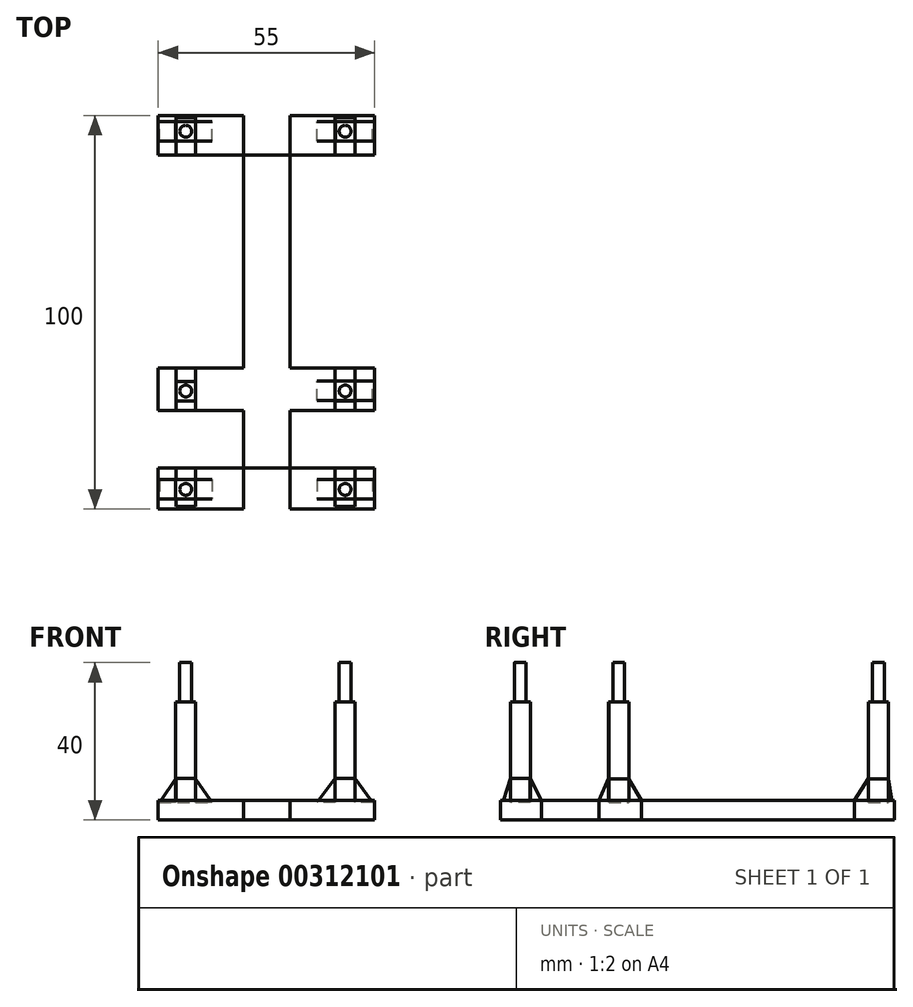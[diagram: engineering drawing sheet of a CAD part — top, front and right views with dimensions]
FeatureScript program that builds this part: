
annotation { "Feature Type Name" : "Feature", "Feature Type Description" : "" }
export const myFeature = defineFeature(function(context is Context, id is Id, definition is map)
    precondition{}
    {
        {
            var Q0;
            Q0=qCreatedBy(makeId("Top.planeOp"),FACE);
            var sketch = newSketch(context, id + "F0", { "sketchPlane" : qUnion([Q0])});
            skLineSegment(sketch, "E0.bottom", {"start": v(27.5, -50) * mm, "end": v(-27.5, -50) * mm});
            skLineSegment(sketch, "E0.top", {"start": v(27.5, 50) * mm, "end": v(-27.5, 50) * mm});
            skLineSegment(sketch, "E0.left", {"start": v(27.5, -50) * mm, "end": v(27.5, 50) * mm});
            skLineSegment(sketch, "E0.right", {"start": v(-27.5, -50) * mm, "end": v(-27.5, 50) * mm});
            skPoint(sketch, "E0.middle", {"position": v(0, 0) * mm});
            skCircle(sketch, "E1", {"center": v(-20.5, -45) * mm, "radius": 1.5 * mm});
            skCircle(sketch, "E2", {"center": v(20, -45) * mm, "radius": 1.5 * mm});
            skCircle(sketch, "E3", {"center": v(-20.5, -20) * mm, "radius": 1.5 * mm});
            skCircle(sketch, "E4", {"center": v(20, -20) * mm, "radius": 1.5 * mm});
            skCircle(sketch, "E5", {"center": v(20, 46) * mm, "radius": 1.5 * mm});
            skCircle(sketch, "E6", {"center": v(-20.5, 46) * mm, "radius": 1.5 * mm});
            skLineSegment(sketch, "E7.bottom", {"start": v(-18, 43.5) * mm, "end": v(-23, 43.5) * mm});
            skLineSegment(sketch, "E7.top", {"start": v(-18, 48.5) * mm, "end": v(-23, 48.5) * mm});
            skLineSegment(sketch, "E7.left", {"start": v(-18, 43.5) * mm, "end": v(-18, 48.5) * mm});
            skLineSegment(sketch, "E7.right", {"start": v(-23, 43.5) * mm, "end": v(-23, 48.5) * mm});
            skLineSegment(sketch, "E8.bottom", {"start": v(22.52, 43.5) * mm, "end": v(17.52, 43.5) * mm});
            skLineSegment(sketch, "E8.top", {"start": v(22.52, 48.5) * mm, "end": v(17.52, 48.5) * mm});
            skLineSegment(sketch, "E8.left", {"start": v(22.52, 43.5) * mm, "end": v(22.52, 48.5) * mm});
            skLineSegment(sketch, "E8.right", {"start": v(17.52, 43.5) * mm, "end": v(17.52, 48.5) * mm});
            skLineSegment(sketch, "E9.bottom", {"start": v(22.5, -22.45) * mm, "end": v(17.5, -22.45) * mm});
            skLineSegment(sketch, "E9.top", {"start": v(22.5, -17.45) * mm, "end": v(17.5, -17.45) * mm});
            skLineSegment(sketch, "E9.left", {"start": v(22.5, -22.45) * mm, "end": v(22.5, -17.45) * mm});
            skLineSegment(sketch, "E9.right", {"start": v(17.5, -22.45) * mm, "end": v(17.5, -17.45) * mm});
            skLineSegment(sketch, "E10.bottom", {"start": v(22.47, -47.44) * mm, "end": v(17.47, -47.44) * mm});
            skLineSegment(sketch, "E10.top", {"start": v(22.47, -42.44) * mm, "end": v(17.47, -42.44) * mm});
            skLineSegment(sketch, "E10.left", {"start": v(22.47, -47.44) * mm, "end": v(22.47, -42.44) * mm});
            skLineSegment(sketch, "E10.right", {"start": v(17.47, -47.44) * mm, "end": v(17.47, -42.44) * mm});
            skLineSegment(sketch, "E11.bottom", {"start": v(-18.04, -47.49) * mm, "end": v(-23.04, -47.49) * mm});
            skLineSegment(sketch, "E11.top", {"start": v(-18.04, -42.49) * mm, "end": v(-23.04, -42.49) * mm});
            skLineSegment(sketch, "E11.left", {"start": v(-18.04, -47.49) * mm, "end": v(-18.04, -42.49) * mm});
            skLineSegment(sketch, "E11.right", {"start": v(-23.04, -47.49) * mm, "end": v(-23.04, -42.49) * mm});
            skLineSegment(sketch, "E12.bottom", {"start": v(-17.97, -22.57) * mm, "end": v(-22.97, -22.57) * mm});
            skLineSegment(sketch, "E12.top", {"start": v(-17.97, -17.57) * mm, "end": v(-22.97, -17.57) * mm});
            skLineSegment(sketch, "E12.left", {"start": v(-17.97, -22.57) * mm, "end": v(-17.97, -17.57) * mm});
            skLineSegment(sketch, "E12.right", {"start": v(-22.97, -22.57) * mm, "end": v(-22.97, -17.57) * mm});
            skLineSegment(sketch, "E13.bottom", {"start": v(-27.5, 50) * mm, "end": v(27.5, 50) * mm});
            skLineSegment(sketch, "E13.top", {"start": v(-27.5, 39.93) * mm, "end": v(27.5, 39.93) * mm});
            skLineSegment(sketch, "E13.left", {"start": v(-27.5, 50) * mm, "end": v(-27.5, 39.93) * mm});
            skLineSegment(sketch, "E13.right", {"start": v(27.5, 50) * mm, "end": v(27.5, 39.93) * mm});
            skLineSegment(sketch, "E14.bottom", {"start": v(-27.5, -50) * mm, "end": v(27.5, -50) * mm});
            skLineSegment(sketch, "E14.top", {"start": v(-27.5, -39.6) * mm, "end": v(27.5, -39.6) * mm});
            skLineSegment(sketch, "E14.left", {"start": v(-27.5, -50) * mm, "end": v(-27.5, -39.6) * mm});
            skLineSegment(sketch, "E14.right", {"start": v(27.5, -50) * mm, "end": v(27.5, -39.6) * mm});
            skLineSegment(sketch, "E15.bottom", {"start": v(-27.5, -14.17) * mm, "end": v(27.5, -14.17) * mm});
            skLineSegment(sketch, "E15.top", {"start": v(-27.5, -25) * mm, "end": v(27.5, -25) * mm});
            skLineSegment(sketch, "E15.left", {"start": v(-27.5, -14.17) * mm, "end": v(-27.5, -25) * mm});
            skLineSegment(sketch, "E15.right", {"start": v(27.5, -14.17) * mm, "end": v(27.5, -25) * mm});
            skLineSegment(sketch, "E16.bottom", {"start": v(-5.85, 50) * mm, "end": v(5.97, 50) * mm});
            skLineSegment(sketch, "E16.top", {"start": v(-5.85, -50) * mm, "end": v(5.97, -50) * mm});
            skLineSegment(sketch, "E16.left", {"start": v(-5.85, 50) * mm, "end": v(-5.85, -50) * mm});
            skLineSegment(sketch, "E16.right", {"start": v(5.97, 50) * mm, "end": v(5.97, -50) * mm});
            skLineSegment(sketch, "E17.bottom", {"start": v(-21.26, 39.93) * mm, "end": v(-27.5, 39.93) * mm});
            skLineSegment(sketch, "E17.top", {"start": v(-21.26, -14.17) * mm, "end": v(-27.5, -14.17) * mm});
            skLineSegment(sketch, "E17.left", {"start": v(-21.26, 39.93) * mm, "end": v(-21.26, -14.17) * mm});
            skLineSegment(sketch, "E17.right", {"start": v(-27.5, 39.93) * mm, "end": v(-27.5, -14.17) * mm});
            skLineSegment(sketch, "E18.bottom", {"start": v(27.5, -14.17) * mm, "end": v(21.08, -14.17) * mm});
            skLineSegment(sketch, "E18.top", {"start": v(27.5, 39.93) * mm, "end": v(21.08, 39.93) * mm});
            skLineSegment(sketch, "E18.left", {"start": v(27.5, -14.17) * mm, "end": v(27.5, 39.93) * mm});
            skLineSegment(sketch, "E18.right", {"start": v(21.08, -14.17) * mm, "end": v(21.08, 39.93) * mm});
            skLineSegment(sketch, "E19.bottom", {"start": v(21.08, -25) * mm, "end": v(27.5, -25) * mm});
            skLineSegment(sketch, "E19.top", {"start": v(21.08, -39.6) * mm, "end": v(27.5, -39.6) * mm});
            skLineSegment(sketch, "E19.left", {"start": v(21.08, -25) * mm, "end": v(21.08, -39.6) * mm});
            skLineSegment(sketch, "E19.right", {"start": v(27.5, -25) * mm, "end": v(27.5, -39.6) * mm});
            skLineSegment(sketch, "E20.bottom", {"start": v(-20.5, -39.6) * mm, "end": v(-27.5, -39.6) * mm});
            skLineSegment(sketch, "E20.top", {"start": v(-20.5, -25) * mm, "end": v(-27.5, -25) * mm});
            skLineSegment(sketch, "E20.left", {"start": v(-20.5, -39.6) * mm, "end": v(-20.5, -25) * mm});
            skLineSegment(sketch, "E20.right", {"start": v(-27.5, -39.6) * mm, "end": v(-27.5, -25) * mm});
            skSolve(sketch);
        }
        {
            var Q0;
            Q0=makeQuery(id+"F0.imprint","IMPRINT",FACE,{"disambiguationData":[TD([[makeQuery(id+"F0.imprint","IMPRINT",EDGE,{"derivedFrom":sQuery(id+"F0.wireOp",EDGE,"E17.bottom")}),1.0]])]});
            var Q1;
            Q1=makeQuery(id+"F0.imprint","IMPRINT",FACE,{"disambiguationData":[TD([[makeQuery(id+"F0.imprint","IMPRINT",EDGE,{"derivedFrom":sQuery(id+"F0.wireOp",EDGE,"E7.bottom")}),1.0]])]});
            var Q2;
            {var subQ5=sQuery(id+"F0.wireOp",EDGE,"E16.bottom");Q2=makeQuery(id+"F0.imprint","IMPRINT",FACE,{"disambiguationData":[TD([[makeQuery(id+"F0.imprint","IMPRINT",EDGE,{"derivedFrom":subQ5}),-1.0]])]});}
            var Q3;
            Q3=makeQuery(id+"F0.imprint","IMPRINT",FACE,{"disambiguationData":[TD([[makeQuery(id+"F0.imprint","IMPRINT",EDGE,{"derivedFrom":sQuery(id+"F0.wireOp",EDGE,"E8.bottom")}),1.0]])]});
            var Q4;
            Q4=makeQuery(id+"F0.imprint","IMPRINT",FACE,{"disambiguationData":[TD([[makeQuery(id+"F0.imprint","IMPRINT",EDGE,{"derivedFrom":sQuery(id+"F0.wireOp",EDGE,"E18.bottom")}),-1.0]])]});
            var Q5;
            {var subQ0=sQuery(id+"F0.wireOp",EDGE,"E16.left");var subQ1=sQuery(id+"F0.wireOp",EDGE,"E13.top");var subQ2=makeQuery(id+"F0.imprint","INTERSECT",VERTEX,{"derivedFrom":[subQ1,subQ0]});Q5=makeQuery(id+"F0.imprint","IMPRINT",FACE,{"disambiguationData":[TD([[makeQuery(id+"F0.imprint","IMPRINT",EDGE,{"disambiguationData":[TD([[subQ2,-1.0]])],"derivedFrom":subQ1}),-1.0]])]});}
            var Q6;
            {var subQ0=sQuery(id+"F0.wireOp",EDGE,"E16.left");var subQ1=sQuery(id+"F0.wireOp",EDGE,"E15.bottom");var subQ2=makeQuery(id+"F0.imprint","INTERSECT",VERTEX,{"derivedFrom":[subQ1,subQ0]});Q6=makeQuery(id+"F0.imprint","IMPRINT",FACE,{"disambiguationData":[TD([[makeQuery(id+"F0.imprint","IMPRINT",EDGE,{"disambiguationData":[TD([[subQ2,-1.0]])],"derivedFrom":subQ1}),-1.0]])]});}
            var Q7;
            {var subQ0=sQuery(id+"F0.wireOp",EDGE,"E16.left");var subQ1=sQuery(id+"F0.wireOp",EDGE,"E14.top");var subQ2=makeQuery(id+"F0.imprint","INTERSECT",VERTEX,{"derivedFrom":[subQ1,subQ0]});Q7=makeQuery(id+"F0.imprint","IMPRINT",FACE,{"disambiguationData":[TD([[makeQuery(id+"F0.imprint","IMPRINT",EDGE,{"disambiguationData":[TD([[subQ2,-1.0]])],"derivedFrom":subQ1}),1.0]])]});}
            var Q8;
            {var subQ5=sQuery(id+"F0.wireOp",EDGE,"E16.top");Q8=makeQuery(id+"F0.imprint","IMPRINT",FACE,{"disambiguationData":[TD([[makeQuery(id+"F0.imprint","IMPRINT",EDGE,{"derivedFrom":subQ5}),1.0]])]});}
            var Q9;
            Q9=makeQuery(id+"F0.imprint","IMPRINT",FACE,{"disambiguationData":[TD([[makeQuery(id+"F0.imprint","IMPRINT",EDGE,{"derivedFrom":sQuery(id+"F0.wireOp",EDGE,"E10.bottom")}),1.0]])]});
            var Q10;
            Q10=makeQuery(id+"F0.imprint","IMPRINT",FACE,{"disambiguationData":[TD([[makeQuery(id+"F0.imprint","IMPRINT",EDGE,{"derivedFrom":sQuery(id+"F0.wireOp",EDGE,"E11.bottom")}),1.0]])]});
            var Q11;
            Q11=makeQuery(id+"F0.imprint","IMPRINT",FACE,{"disambiguationData":[TD([[makeQuery(id+"F0.imprint","IMPRINT",EDGE,{"derivedFrom":sQuery(id+"F0.wireOp",EDGE,"E20.bottom")}),-1.0]])]});
            var Q12;
            Q12=makeQuery(id+"F0.imprint","IMPRINT",FACE,{"disambiguationData":[TD([[makeQuery(id+"F0.imprint","IMPRINT",EDGE,{"derivedFrom":sQuery(id+"F0.wireOp",EDGE,"E19.bottom")}),-1.0]])]});
            var Q13;
            Q13=makeQuery(id+"F0.imprint","IMPRINT",FACE,{"disambiguationData":[TD([[makeQuery(id+"F0.imprint","IMPRINT",EDGE,{"derivedFrom":sQuery(id+"F0.wireOp",EDGE,"E9.bottom")}),1.0]])]});
            var Q14;
            Q14=makeQuery(id+"F0.imprint","IMPRINT",FACE,{"disambiguationData":[TD([[makeQuery(id+"F0.imprint","IMPRINT",EDGE,{"derivedFrom":sQuery(id+"F0.wireOp",EDGE,"E12.bottom")}),1.0]])]});
            extrude(context, id + "F1", {"entities" : qUnion([Q0, Q1, Q2, Q3, Q4, Q5, Q6, Q7, Q8, Q9, Q10, Q11, Q12, Q13, Q14]), "depth" : 5 * mm});
        }
        {
            var Q0;
            Q0=makeQuery(id+"F0.imprint","IMPRINT",FACE,{"disambiguationData":[TD([[makeQuery(id+"F0.imprint","IMPRINT",EDGE,{"derivedFrom":sQuery(id+"F0.wireOp",EDGE,"E6")}),-1.0]])]});
            var Q1;
            Q1=makeQuery(id+"F0.imprint","IMPRINT",FACE,{"disambiguationData":[TD([[makeQuery(id+"F0.imprint","IMPRINT",EDGE,{"derivedFrom":sQuery(id+"F0.wireOp",EDGE,"E5")}),-1.0]])]});
            var Q2;
            Q2=makeQuery(id+"F0.imprint","IMPRINT",FACE,{"disambiguationData":[TD([[makeQuery(id+"F0.imprint","IMPRINT",EDGE,{"derivedFrom":sQuery(id+"F0.wireOp",EDGE,"E3")}),-1.0]])]});
            var Q3;
            Q3=makeQuery(id+"F0.imprint","IMPRINT",FACE,{"disambiguationData":[TD([[makeQuery(id+"F0.imprint","IMPRINT",EDGE,{"derivedFrom":sQuery(id+"F0.wireOp",EDGE,"E4")}),-1.0]])]});
            var Q4;
            Q4=makeQuery(id+"F0.imprint","IMPRINT",FACE,{"disambiguationData":[TD([[makeQuery(id+"F0.imprint","IMPRINT",EDGE,{"derivedFrom":sQuery(id+"F0.wireOp",EDGE,"E2")}),-1.0]])]});
            var Q5;
            Q5=makeQuery(id+"F0.imprint","IMPRINT",FACE,{"disambiguationData":[TD([[makeQuery(id+"F0.imprint","IMPRINT",EDGE,{"derivedFrom":sQuery(id+"F0.wireOp",EDGE,"E1")}),-1.0]])]});
            extrude(context, id + "F2", {"entities" : qUnion([Q0, Q1, Q2, Q3, Q4, Q5]), "operationType" : NewBodyOperationType.ADD, "depth" : 30 * mm});
        }
        {
            var Q0;
            Q0=makeQuery(id+"F0.imprint","IMPRINT",FACE,{"disambiguationData":[TD([[makeQuery(id+"F0.imprint","IMPRINT",EDGE,{"derivedFrom":sQuery(id+"F0.wireOp",EDGE,"E6")}),1.0]])]});
            var Q1;
            Q1=makeQuery(id+"F0.imprint","IMPRINT",FACE,{"disambiguationData":[TD([[makeQuery(id+"F0.imprint","IMPRINT",EDGE,{"derivedFrom":sQuery(id+"F0.wireOp",EDGE,"E5")}),1.0]])]});
            var Q2;
            Q2=makeQuery(id+"F0.imprint","IMPRINT",FACE,{"disambiguationData":[TD([[makeQuery(id+"F0.imprint","IMPRINT",EDGE,{"derivedFrom":sQuery(id+"F0.wireOp",EDGE,"E4")}),1.0]])]});
            var Q3;
            Q3=makeQuery(id+"F0.imprint","IMPRINT",FACE,{"disambiguationData":[TD([[makeQuery(id+"F0.imprint","IMPRINT",EDGE,{"derivedFrom":sQuery(id+"F0.wireOp",EDGE,"E3")}),1.0]])]});
            var Q4;
            Q4=makeQuery(id+"F0.imprint","IMPRINT",FACE,{"disambiguationData":[TD([[makeQuery(id+"F0.imprint","IMPRINT",EDGE,{"derivedFrom":sQuery(id+"F0.wireOp",EDGE,"E1")}),1.0]])]});
            var Q5;
            Q5=makeQuery(id+"F0.imprint","IMPRINT",FACE,{"disambiguationData":[TD([[makeQuery(id+"F0.imprint","IMPRINT",EDGE,{"derivedFrom":sQuery(id+"F0.wireOp",EDGE,"E2")}),1.0]])]});
            extrude(context, id + "F3", {"entities" : qUnion([Q0, Q1, Q2, Q3, Q4, Q5]), "operationType" : NewBodyOperationType.ADD, "depth" : 40 * mm});
        }
        {
            var Q0;
            Q0=makeQuery(id+"F2.opExtrude","SWEPT_FACE",FACE,{"disambiguationData":[OSD([sQuery(id+"F0.wireOp",EDGE,"E11.bottom")])]});
            var sketch = newSketch(context, id + "F4", { "sketchPlane" : qUnion([Q0])});
            skLineSegment(sketch, "E21", {"start": v(-23.04, 10.44) * mm, "end": v(-27.17, 4.44) * mm});
            skLineSegment(sketch, "E22", {"start": v(-27.17, 4.44) * mm, "end": v(-23.04, 4.44) * mm});
            skLineSegment(sketch, "E23", {"start": v(-23.04, 10.44) * mm, "end": v(-18.04, 10.44) * mm});
            skLineSegment(sketch, "E24", {"start": v(-18.04, 10.44) * mm, "end": v(-13.84, 4.44) * mm});
            skLineSegment(sketch, "E25", {"start": v(-13.84, 4.44) * mm, "end": v(-18.04, 4.44) * mm});
            skLineSegment(sketch, "E26", {"start": v(-18.04, 4.44) * mm, "end": v(-23.04, 4.44) * mm});
            skLineSegment(sketch, "E27.0.0", {"start": v(17.47, 0) * mm, "end": v(22.47, 0) * mm});
            skLineSegment(sketch, "E27.0.1", {"start": v(22.47, 0) * mm, "end": v(22.47, 30) * mm});
            skLineSegment(sketch, "E27.0.2", {"start": v(22.47, 30) * mm, "end": v(17.47, 30) * mm});
            skLineSegment(sketch, "E27.0.3", {"start": v(17.47, 30) * mm, "end": v(17.47, 0) * mm});
            skLineSegment(sketch, "E28", {"start": v(22.47, 10.52) * mm, "end": v(27.02, 4.5) * mm});
            skLineSegment(sketch, "E29", {"start": v(27.02, 4.5) * mm, "end": v(12.84, 4.5) * mm});
            skLineSegment(sketch, "E30", {"start": v(12.84, 4.5) * mm, "end": v(17.47, 10.52) * mm});
            skLineSegment(sketch, "E31", {"start": v(17.47, 10.52) * mm, "end": v(22.47, 10.52) * mm});
            skSolve(sketch);
        }
        {
            var Q0;
            {var subQ0=sQuery(id+"F4.wireOp",EDGE,"E21");Q0=makeQuery(id+"F4.imprint","IMPRINT",FACE,{"disambiguationData":[TD([[makeQuery(id+"F4.imprint","IMPRINT",EDGE,{"derivedFrom":subQ0}),1.0]])]});}
            var Q1;
            {var subQ0=sQuery(id+"F4.wireOp",EDGE,"E24");Q1=makeQuery(id+"F4.imprint","IMPRINT",FACE,{"disambiguationData":[TD([[makeQuery(id+"F4.imprint","IMPRINT",EDGE,{"derivedFrom":subQ0}),-1.0]])]});}
            var Q2;
            {var subQ0=sQuery(id+"F4.wireOp",EDGE,"E30");Q2=makeQuery(id+"F4.imprint","IMPRINT",FACE,{"disambiguationData":[TD([[makeQuery(id+"F4.imprint","IMPRINT",EDGE,{"derivedFrom":subQ0}),-1.0]])]});}
            var Q3;
            {var subQ0=sQuery(id+"F4.wireOp",EDGE,"E28");Q3=makeQuery(id+"F4.imprint","IMPRINT",FACE,{"disambiguationData":[TD([[makeQuery(id+"F4.imprint","IMPRINT",EDGE,{"derivedFrom":subQ0}),-1.0]])]});}
            extrude(context, id + "F5", {"entities" : qUnion([Q0, Q1, Q2, Q3]), "depth" : -5 * mm});
        }
        {
            var Q0;
            Q0=makeQuery(id+"F2.opExtrude","SWEPT_FACE",FACE,{"disambiguationData":[OSD([sQuery(id+"F0.wireOp",EDGE,"E7.right")])]});
            var sketch = newSketch(context, id + "F6", { "sketchPlane" : qUnion([Q0])});
            skLineSegment(sketch, "E32.0.0", {"start": v(17.57, 0) * mm, "end": v(22.57, 0) * mm});
            skLineSegment(sketch, "E32.0.1", {"start": v(22.57, 0) * mm, "end": v(22.57, 30) * mm});
            skLineSegment(sketch, "E32.0.2", {"start": v(22.57, 30) * mm, "end": v(17.57, 30) * mm});
            skLineSegment(sketch, "E32.0.3", {"start": v(17.57, 30) * mm, "end": v(17.57, 0) * mm});
            skLineSegment(sketch, "E33.0.0", {"start": v(42.49, 0) * mm, "end": v(47.49, 0) * mm});
            skLineSegment(sketch, "E33.0.1", {"start": v(47.49, 0) * mm, "end": v(47.49, 30) * mm});
            skLineSegment(sketch, "E33.0.2", {"start": v(47.49, 30) * mm, "end": v(42.49, 30) * mm});
            skLineSegment(sketch, "E33.0.3", {"start": v(42.49, 30) * mm, "end": v(42.49, 0) * mm});
            skLineSegment(sketch, "E34", {"start": v(47.49, 10.55) * mm, "end": v(-48.5, 10.55) * mm});
            skLineSegment(sketch, "E35", {"start": v(-48.5, 10.55) * mm, "end": v(-49.41, 5) * mm});
            skLineSegment(sketch, "E36", {"start": v(-49.41, 5) * mm, "end": v(49.29, 5) * mm});
            skLineSegment(sketch, "E37", {"start": v(49.29, 5) * mm, "end": v(47.49, 10.55) * mm});
            skLineSegment(sketch, "E38", {"start": v(42.49, 10.55) * mm, "end": v(39.6, 5) * mm});
            skLineSegment(sketch, "E39", {"start": v(22.57, 10.55) * mm, "end": v(25, 5) * mm});
            skLineSegment(sketch, "E40", {"start": v(17.57, 10.55) * mm, "end": v(14.17, 5) * mm});
            skLineSegment(sketch, "E41", {"start": v(-43.5, 10.55) * mm, "end": v(-39.93, 5) * mm});
            skLineSegment(sketch, "E42.0.0", {"start": v(-39.93, 0) * mm, "end": v(14.17, 0) * mm});
            skLineSegment(sketch, "E42.0.1", {"start": v(14.17, 0) * mm, "end": v(14.17, 5) * mm});
            skLineSegment(sketch, "E42.0.2", {"start": v(14.17, 5) * mm, "end": v(-39.93, 5) * mm});
            skLineSegment(sketch, "E42.0.3", {"start": v(-39.93, 5) * mm, "end": v(-39.93, 0) * mm});
            skLineSegment(sketch, "E43.0.0", {"start": v(25, 0) * mm, "end": v(39.6, 0) * mm});
            skLineSegment(sketch, "E43.0.1", {"start": v(39.6, 0) * mm, "end": v(39.6, 5) * mm});
            skLineSegment(sketch, "E43.0.2", {"start": v(39.6, 5) * mm, "end": v(25, 5) * mm});
            skLineSegment(sketch, "E43.0.3", {"start": v(25, 5) * mm, "end": v(25, 0) * mm});
            skSolve(sketch);
        }
        {
            var Q0;
            {var subQ0=sQuery(id+"F6.wireOp",EDGE,"E37");Q0=makeQuery(id+"F6.imprint","IMPRINT",FACE,{"disambiguationData":[TD([[makeQuery(id+"F6.imprint","IMPRINT",EDGE,{"derivedFrom":subQ0}),1.0]])]});}
            var Q1;
            {var subQ0=sQuery(id+"F6.wireOp",EDGE,"E38");Q1=makeQuery(id+"F6.imprint","IMPRINT",FACE,{"disambiguationData":[TD([[makeQuery(id+"F6.imprint","IMPRINT",EDGE,{"derivedFrom":subQ0}),1.0]])]});}
            var Q2;
            {var subQ0=sQuery(id+"F6.wireOp",EDGE,"E39");Q2=makeQuery(id+"F6.imprint","IMPRINT",FACE,{"disambiguationData":[TD([[makeQuery(id+"F6.imprint","IMPRINT",EDGE,{"derivedFrom":subQ0}),-1.0]])]});}
            var Q3;
            {var subQ0=sQuery(id+"F6.wireOp",EDGE,"E40");Q3=makeQuery(id+"F6.imprint","IMPRINT",FACE,{"disambiguationData":[TD([[makeQuery(id+"F6.imprint","IMPRINT",EDGE,{"derivedFrom":subQ0}),1.0]])]});}
            var Q4;
            {var subQ0=sQuery(id+"F6.wireOp",EDGE,"E41");Q4=makeQuery(id+"F6.imprint","IMPRINT",FACE,{"disambiguationData":[TD([[makeQuery(id+"F6.imprint","IMPRINT",EDGE,{"derivedFrom":subQ0}),-1.0]])]});}
            var Q5;
            {var subQ0=sQuery(id+"F6.wireOp",EDGE,"E35");Q5=makeQuery(id+"F6.imprint","IMPRINT",FACE,{"disambiguationData":[TD([[makeQuery(id+"F6.imprint","IMPRINT",EDGE,{"derivedFrom":subQ0}),1.0]])]});}
            extrude(context, id + "F7", {"entities" : qUnion([Q0, Q1, Q2, Q3, Q4, Q5]), "depth" : -5 * mm});
        }
        {
            var Q0;
            Q0=makeQuery(id+"F2.opExtrude","SWEPT_FACE",FACE,{"disambiguationData":[OSD([sQuery(id+"F0.wireOp",EDGE,"E10.left")])]});
            var sketch = newSketch(context, id + "F8", { "sketchPlane" : qUnion([Q0])});
            skLineSegment(sketch, "E44.0.0", {"start": v(-47.49, 5) * mm, "end": v(-47.49, 10.55) * mm});
            skLineSegment(sketch, "E44.0.1", {"start": v(-47.49, 10.55) * mm, "end": v(-49.29, 5) * mm});
            skLineSegment(sketch, "E44.0.2", {"start": v(-49.29, 5) * mm, "end": v(-47.49, 5) * mm});
            skLineSegment(sketch, "E45.0.0", {"start": v(-42.49, 10.55) * mm, "end": v(-42.49, 5) * mm});
            skLineSegment(sketch, "E45.0.1", {"start": v(-42.49, 5) * mm, "end": v(-39.6, 5) * mm});
            skLineSegment(sketch, "E45.0.2", {"start": v(-39.6, 5) * mm, "end": v(-42.49, 10.55) * mm});
            skLineSegment(sketch, "E46.0.0", {"start": v(-22.57, 5) * mm, "end": v(-22.57, 10.55) * mm});
            skLineSegment(sketch, "E46.0.1", {"start": v(-22.57, 10.55) * mm, "end": v(-25, 5) * mm});
            skLineSegment(sketch, "E46.0.2", {"start": v(-25, 5) * mm, "end": v(-22.57, 5) * mm});
            skLineSegment(sketch, "E47.0.0", {"start": v(-17.57, 10.55) * mm, "end": v(-17.57, 5) * mm});
            skLineSegment(sketch, "E47.0.1", {"start": v(-17.57, 5) * mm, "end": v(-14.17, 5) * mm});
            skLineSegment(sketch, "E47.0.2", {"start": v(-14.17, 5) * mm, "end": v(-17.57, 10.55) * mm});
            skLineSegment(sketch, "E48.0.0", {"start": v(43.5, 5) * mm, "end": v(43.5, 10.55) * mm});
            skLineSegment(sketch, "E48.0.1", {"start": v(43.5, 10.55) * mm, "end": v(39.93, 5) * mm});
            skLineSegment(sketch, "E48.0.2", {"start": v(39.93, 5) * mm, "end": v(43.5, 5) * mm});
            skLineSegment(sketch, "E49.0.0", {"start": v(49.41, 5) * mm, "end": v(48.5, 10.55) * mm});
            skLineSegment(sketch, "E49.0.1", {"start": v(48.5, 10.55) * mm, "end": v(48.5, 5) * mm});
            skLineSegment(sketch, "E49.0.2", {"start": v(48.5, 5) * mm, "end": v(49.41, 5) * mm});
            skLineSegment(sketch, "E50.0.0", {"start": v(-14.17, 0) * mm, "end": v(39.93, 0) * mm});
            skLineSegment(sketch, "E50.0.1", {"start": v(39.93, 0) * mm, "end": v(39.93, 5) * mm});
            skLineSegment(sketch, "E50.0.2", {"start": v(39.93, 5) * mm, "end": v(-14.17, 5) * mm});
            skLineSegment(sketch, "E50.0.3", {"start": v(-14.17, 5) * mm, "end": v(-14.17, 0) * mm});
            skLineSegment(sketch, "E51.0.0", {"start": v(-39.6, 0) * mm, "end": v(-25, 0) * mm});
            skLineSegment(sketch, "E51.0.1", {"start": v(-25, 0) * mm, "end": v(-25, 5) * mm});
            skLineSegment(sketch, "E51.0.2", {"start": v(-25, 5) * mm, "end": v(-39.6, 5) * mm});
            skLineSegment(sketch, "E51.0.3", {"start": v(-39.6, 5) * mm, "end": v(-39.6, 0) * mm});
            skSolve(sketch);
        }
        {
            var Q0;
            Q0=makeQuery(id+"F8.imprint","IMPRINT",FACE,{"disambiguationData":[TD([[makeQuery(id+"F8.imprint","IMPRINT",EDGE,{"derivedFrom":sQuery(id+"F8.wireOp",EDGE,"E44.0.0")}),1.0]])]});
            var Q1;
            {var subQ1=sQuery(id+"F8.wireOp",EDGE,"E45.0.1");var subQ3=makeQuery(id+"F2.opExtrude","SWEPT_EDGE",EDGE,{"disambiguationData":[OSD([sQuery(id+"F0.wireOp",EDGE,"E10.top"),sQuery(id+"F0.wireOp",EDGE,"E10.left")])]});var subQ4=makeQuery(id+"F8.imprint","INTERSECT",VERTEX,{"derivedFrom":[subQ3,subQ1]});Q1=makeQuery(id+"F8.imprint","IMPRINT",FACE,{"disambiguationData":[TD([[makeQuery(id+"F8.imprint","IMPRINT",EDGE,{"disambiguationData":[TD([[subQ4,-1.0]])],"derivedFrom":subQ1}),1.0]])]});}
            var Q2;
            Q2=makeQuery(id+"F8.imprint","IMPRINT",FACE,{"disambiguationData":[TD([[makeQuery(id+"F8.imprint","IMPRINT",EDGE,{"derivedFrom":sQuery(id+"F8.wireOp",EDGE,"E46.0.0")}),1.0]])]});
            var Q3;
            Q3=makeQuery(id+"F8.imprint","IMPRINT",FACE,{"disambiguationData":[TD([[makeQuery(id+"F8.imprint","IMPRINT",EDGE,{"derivedFrom":sQuery(id+"F8.wireOp",EDGE,"E47.0.0")}),1.0]])]});
            var Q4;
            Q4=makeQuery(id+"F8.imprint","IMPRINT",FACE,{"disambiguationData":[TD([[makeQuery(id+"F8.imprint","IMPRINT",EDGE,{"derivedFrom":sQuery(id+"F8.wireOp",EDGE,"E48.0.0")}),1.0]])]});
            var Q5;
            Q5=makeQuery(id+"F8.imprint","IMPRINT",FACE,{"disambiguationData":[TD([[makeQuery(id+"F8.imprint","IMPRINT",EDGE,{"derivedFrom":sQuery(id+"F8.wireOp",EDGE,"E49.0.0")}),1.0]])]});
            extrude(context, id + "F9", {"entities" : qUnion([Q0, Q1, Q2, Q3, Q4, Q5]), "depth" : -5 * mm});
        }
        {
            var Q0;
            Q0=makeQuery(id+"F2.opExtrude","SWEPT_FACE",FACE,{"disambiguationData":[OSD([sQuery(id+"F0.wireOp",EDGE,"E9.top")])]});
            var sketch = newSketch(context, id + "F10", { "sketchPlane" : qUnion([Q0])});
            skLineSegment(sketch, "E52.0.0", {"start": v(-22.47, 10.52) * mm, "end": v(-27.02, 4.5) * mm});
            skLineSegment(sketch, "E52.0.1", {"start": v(-27.02, 4.5) * mm, "end": v(-22.47, 4.5) * mm});
            skLineSegment(sketch, "E52.0.2", {"start": v(-22.47, 4.5) * mm, "end": v(-22.47, 10.52) * mm});
            skLineSegment(sketch, "E53.0.0", {"start": v(-12.84, 4.5) * mm, "end": v(-17.47, 10.52) * mm});
            skLineSegment(sketch, "E53.0.1", {"start": v(-17.47, 10.52) * mm, "end": v(-17.47, 4.5) * mm});
            skLineSegment(sketch, "E53.0.2", {"start": v(-17.47, 4.5) * mm, "end": v(-12.84, 4.5) * mm});
            skLineSegment(sketch, "E54.0.0", {"start": v(13.84, 4.44) * mm, "end": v(13.84, 4.44) * mm});
            skLineSegment(sketch, "E54.0.1", {"start": v(18.04, 4.44) * mm, "end": v(18.04, 10.44) * mm});
            skLineSegment(sketch, "E54.0.2", {"start": v(18.04, 10.44) * mm, "end": v(13.84, 4.44) * mm});
            skLineSegment(sketch, "E55.0.0", {"start": v(27.17, 4.44) * mm, "end": v(23.04, 10.44) * mm});
            skLineSegment(sketch, "E55.0.1", {"start": v(23.04, 10.44) * mm, "end": v(23.04, 5) * mm});
            skLineSegment(sketch, "E55.0.2", {"start": v(23.04, 4.44) * mm, "end": v(27.17, 4.44) * mm});
            skSolve(sketch);
        }
        {
            var Q0;
            {var subQ0=sQuery(id+"F10.wireOp",EDGE,"E52.0.1");var subQ1=sQuery(id+"F10.wireOp",EDGE,"E52.0.0");var subQ2=makeQuery(id+"F10.imprint","INTERSECT",VERTEX,{"derivedFrom":[subQ1,subQ0]});Q0=makeQuery(id+"F10.imprint","IMPRINT",FACE,{"disambiguationData":[TD([[makeQuery(id+"F10.imprint","IMPRINT",EDGE,{"disambiguationData":[TD([[subQ2,1.0]])],"derivedFrom":subQ1}),1.0]])]});}
            var Q1;
            Q1=makeQuery(id+"F10.imprint","IMPRINT",FACE,{"disambiguationData":[TD([[makeQuery(id+"F10.imprint","IMPRINT",EDGE,{"derivedFrom":sQuery(id+"F10.wireOp",EDGE,"E53.0.0")}),1.0]])]});
            var Q2;
            Q2=makeQuery(id+"F10.imprint","IMPRINT",FACE,{"disambiguationData":[TD([[makeQuery(id+"F10.imprint","IMPRINT",EDGE,{"derivedFrom":sQuery(id+"F10.wireOp",EDGE,"E54.0.0")}),1.0]])]});
            var Q3;
            Q3=makeQuery(id+"F10.imprint","IMPRINT",FACE,{"disambiguationData":[TD([[makeQuery(id+"F10.imprint","IMPRINT",EDGE,{"derivedFrom":sQuery(id+"F10.wireOp",EDGE,"E55.0.0")}),1.0]])]});
            extrude(context, id + "F11", {"entities" : qUnion([Q0, Q1, Q2, Q3]), "depth" : -5 * mm});
        }
        {
            var Q0;
            Q0=makeQuery(id+"F2.opExtrude","SWEPT_FACE",FACE,{"disambiguationData":[OSD([sQuery(id+"F0.wireOp",EDGE,"E8.top")])]});
            var sketch = newSketch(context, id + "F12", { "sketchPlane" : qUnion([Q0])});
            skLineSegment(sketch, "E56.0.0", {"start": v(-22.5, 10.49) * mm, "end": v(-27.02, 4.5) * mm});
            skLineSegment(sketch, "E56.0.1", {"start": v(-27.02, 4.5) * mm, "end": v(-22.47, 4.5) * mm});
            skLineSegment(sketch, "E56.0.2", {"start": v(-22.5, 4.5) * mm, "end": v(-22.5, 10.49) * mm});
            skLineSegment(sketch, "E57.0.0", {"start": v(-17.47, 10.52) * mm, "end": v(-17.47, 4.5) * mm});
            skLineSegment(sketch, "E57.0.1", {"start": v(-17.47, 4.5) * mm, "end": v(-12.84, 4.5) * mm});
            skLineSegment(sketch, "E57.0.2", {"start": v(-12.84, 4.5) * mm, "end": v(-17.47, 10.52) * mm});
            skLineSegment(sketch, "E58.0.0", {"start": v(18.04, 4.44) * mm, "end": v(18.04, 10.44) * mm});
            skLineSegment(sketch, "E58.0.1", {"start": v(18.04, 10.44) * mm, "end": v(13.84, 4.44) * mm});
            skLineSegment(sketch, "E58.0.2", {"start": v(13.84, 4.44) * mm, "end": v(18.04, 4.44) * mm});
            skLineSegment(sketch, "E59.0.0", {"start": v(23.04, 10.44) * mm, "end": v(23.04, 4.44) * mm});
            skLineSegment(sketch, "E59.0.1", {"start": v(23.04, 4.44) * mm, "end": v(27.17, 4.44) * mm});
            skLineSegment(sketch, "E59.0.2", {"start": v(27.17, 4.44) * mm, "end": v(23.04, 10.44) * mm});
            skSolve(sketch);
        }
        {
            var Q0;
            {var subQ0=sQuery(id+"F12.wireOp",EDGE,"E56.0.1");var subQ1=sQuery(id+"F12.wireOp",EDGE,"E56.0.0");var subQ2=makeQuery(id+"F12.imprint","INTERSECT",VERTEX,{"derivedFrom":[subQ1,subQ0]});Q0=makeQuery(id+"F12.imprint","IMPRINT",FACE,{"disambiguationData":[TD([[makeQuery(id+"F12.imprint","IMPRINT",EDGE,{"disambiguationData":[TD([[subQ2,1.0]])],"derivedFrom":subQ1}),1.0]])]});}
            var Q1;
            Q1=makeQuery(id+"F12.imprint","IMPRINT",FACE,{"disambiguationData":[TD([[makeQuery(id+"F12.imprint","IMPRINT",EDGE,{"derivedFrom":sQuery(id+"F12.wireOp",EDGE,"E57.0.0")}),1.0]])]});
            var Q2;
            Q2=makeQuery(id+"F12.imprint","IMPRINT",FACE,{"disambiguationData":[TD([[makeQuery(id+"F12.imprint","IMPRINT",EDGE,{"derivedFrom":sQuery(id+"F12.wireOp",EDGE,"E58.0.0")}),1.0]])]});
            var Q3;
            Q3=makeQuery(id+"F12.imprint","IMPRINT",FACE,{"disambiguationData":[TD([[makeQuery(id+"F12.imprint","IMPRINT",EDGE,{"derivedFrom":sQuery(id+"F12.wireOp",EDGE,"E59.0.0")}),1.0]])]});
            extrude(context, id + "F13", {"entities" : qUnion([Q0, Q1, Q2, Q3]), "depth" : -5 * mm});
        }
    });
